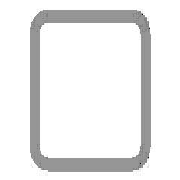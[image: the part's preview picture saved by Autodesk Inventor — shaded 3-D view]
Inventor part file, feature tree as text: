
AUTODESK INVENTOR PART (.ipt)
format: ipt  version: 2022 (Build 260153000, 153)  size: 134,144 bytes
history: native  units: mm (DEFAULTED — no unit token found)
features: other x4, sketch x3, extrude x1, plane x1
ambient origin geometry x8: Origin, YZ Plane, XZ Plane, XY Plane, X Axis, Y Axis, Z Axis, Center Point
bodies: Solid1 (feature_tree)
feature tree (9):
  parser-record x1  (decoder bookkeeping rows leaked as tree rows — omitted from the tree; the rows remain in map.json)
  other  "Driven Length"
  other  "Plano inicial"
  other  "Plano final"
  extrude  "Cuerpo"  TaperAngle=0.0deg  [1 undecoded]
  sketch  "Boceto"  dims[d10=40.0mm d11=40.0mm d12=5.0mm d13=-0.0mm d14=600.0mm d15=20.0mm d16=20.0mm d17=90.0deg d18=600.0mm]
  sketch  "Sketch3"  dims[d3=600.0mm d4=0.0mm]
  plane  "Work Plane3"
  sketch  "Sketch4"  dims[d7=7.5mm]
note: 1 required parameter value undecoded (feature->parameter linkage not recoverable at this tier; creation-order binding heuristic only, values carry confidence <= 0.55)
